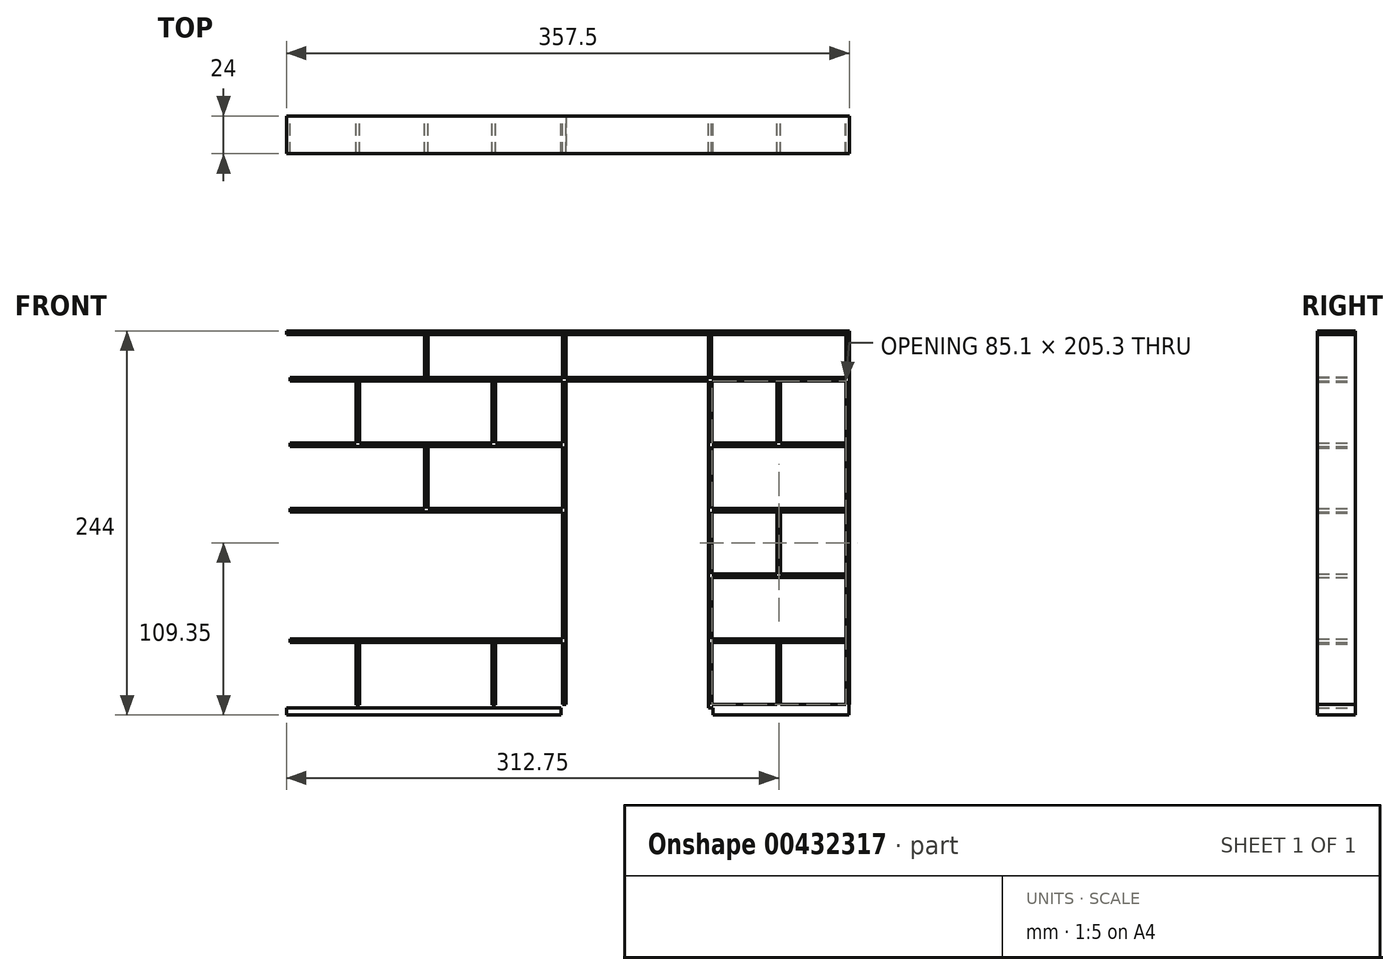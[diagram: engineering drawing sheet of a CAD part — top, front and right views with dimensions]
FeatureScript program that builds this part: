
annotation { "Feature Type Name" : "Feature", "Feature Type Description" : "" }
export const myFeature = defineFeature(function(context is Context, id is Id, definition is map)
    precondition{}
    {
        {
            var Q0;
            Q0=qCreatedBy(makeId("Front.planeOp"),FACE);
            var sketch = newSketch(context, id + "F0", { "sketchPlane" : qUnion([Q0])});
            skLineSegment(sketch, "E0", {"start": v(3.75, 85) * mm, "end": v(3.75, -122) * mm});
            skLineSegment(sketch, "E1", {"start": v(84.25, 85) * mm, "end": v(84.25, -122) * mm});
            skLineSegment(sketch, "E2", {"start": v(3.75, 85) * mm, "end": v(84.25, 85) * mm});
            skLineSegment(sketch, "E3", {"start": v(178.75, 119.8) * mm, "end": v(-178.75, 119.8) * mm});
            skLineSegment(sketch, "E4", {"start": v(-178.75, 119.8) * mm, "end": v(-178.75, 122) * mm});
            skLineSegment(sketch, "E5", {"start": v(-178.75, 122) * mm, "end": v(178.75, 122) * mm});
            skLineSegment(sketch, "E6", {"start": v(178.75, 122) * mm, "end": v(178.75, 119.8) * mm});
            skLineSegment(sketch, "E7", {"start": v(176.55, 90) * mm, "end": v(-176.55, 90) * mm});
            skLineSegment(sketch, "E8", {"start": v(-176.55, 90) * mm, "end": v(-176.55, 92.2) * mm});
            skLineSegment(sketch, "E9", {"start": v(-176.55, 92.2) * mm, "end": v(176.55, 92.2) * mm});
            skLineSegment(sketch, "E10", {"start": v(176.55, 92.2) * mm, "end": v(176.55, 90) * mm});
            skLineSegment(sketch, "E11", {"start": v(-3.45, -76) * mm, "end": v(-176.55, -76) * mm});
            skLineSegment(sketch, "E12", {"start": v(-176.55, -76) * mm, "end": v(-176.55, -73.8) * mm});
            skLineSegment(sketch, "E13", {"start": v(-176.55, -73.8) * mm, "end": v(-3.45, -73.8) * mm});
            skLineSegment(sketch, "E14", {"start": v(-3.45, -73.8) * mm, "end": v(-3.45, -76) * mm});
            skLineSegment(sketch, "E15", {"start": v(-1.25, -117.5) * mm, "end": v(-178.75, -117.5) * mm});
            skLineSegment(sketch, "E16", {"start": v(-178.75, -117.5) * mm, "end": v(-178.75, -115.3) * mm});
            skLineSegment(sketch, "E17", {"start": v(-178.75, -115.3) * mm, "end": v(-1.25, -115.3) * mm});
            skLineSegment(sketch, "E18", {"start": v(-1.25, -115.3) * mm, "end": v(-1.25, -117.5) * mm});
            skLineSegment(sketch, "E19", {"start": v(178.45, -117.5) * mm, "end": v(89.25, -117.5) * mm});
            skLineSegment(sketch, "E20", {"start": v(89.25, -117.5) * mm, "end": v(89.25, -115.3) * mm});
            skLineSegment(sketch, "E21", {"start": v(89.25, -115.3) * mm, "end": v(178.45, -115.3) * mm});
            skLineSegment(sketch, "E22", {"start": v(178.45, -115.3) * mm, "end": v(178.45, -117.5) * mm});
            skLineSegment(sketch, "E23", {"start": v(-176.55, 119.8) * mm, "end": v(-176.55, -115.3) * mm});
            skLineSegment(sketch, "E24", {"start": v(-176.55, -115.3) * mm, "end": v(-178.75, -115.3) * mm});
            skLineSegment(sketch, "E25", {"start": v(-178.75, -115.3) * mm, "end": v(-178.75, 119.8) * mm});
            skLineSegment(sketch, "E26", {"start": v(-178.75, 119.8) * mm, "end": v(-176.55, 119.8) * mm});
            skLineSegment(sketch, "E27", {"start": v(178.75, 119.8) * mm, "end": v(178.75, -115.3) * mm});
            skLineSegment(sketch, "E28", {"start": v(178.75, -115.3) * mm, "end": v(176.55, -115.3) * mm});
            skLineSegment(sketch, "E29", {"start": v(176.55, -115.3) * mm, "end": v(176.55, 119.8) * mm});
            skLineSegment(sketch, "E30", {"start": v(176.55, 119.8) * mm, "end": v(178.75, 119.8) * mm});
            skLineSegment(sketch, "E31", {"start": v(-3.45, 7) * mm, "end": v(-176.55, 7) * mm});
            skLineSegment(sketch, "E32", {"start": v(-176.55, 7) * mm, "end": v(-176.55, 9.2) * mm});
            skLineSegment(sketch, "E33", {"start": v(-176.55, 9.2) * mm, "end": v(-3.45, 9.2) * mm});
            skLineSegment(sketch, "E34", {"start": v(-3.45, 9.2) * mm, "end": v(-3.45, 7) * mm});
            skLineSegment(sketch, "E35", {"start": v(-3.45, 48.5) * mm, "end": v(-176.55, 48.5) * mm});
            skLineSegment(sketch, "E36", {"start": v(-176.55, 48.5) * mm, "end": v(-176.55, 50.7) * mm});
            skLineSegment(sketch, "E37", {"start": v(-176.55, 50.7) * mm, "end": v(-3.45, 50.7) * mm});
            skLineSegment(sketch, "E38", {"start": v(-3.45, 50.7) * mm, "end": v(-3.45, 48.5) * mm});
            skLineSegment(sketch, "E39", {"start": v(176.25, -76) * mm, "end": v(91.45, -76) * mm});
            skLineSegment(sketch, "E40", {"start": v(91.45, -76) * mm, "end": v(91.45, -73.8) * mm});
            skLineSegment(sketch, "E41", {"start": v(91.45, -73.8) * mm, "end": v(176.25, -73.8) * mm});
            skLineSegment(sketch, "E42", {"start": v(176.25, -73.8) * mm, "end": v(176.25, -76) * mm});
            skLineSegment(sketch, "E43", {"start": v(176.25, -34.5) * mm, "end": v(91.45, -34.5) * mm});
            skLineSegment(sketch, "E44", {"start": v(91.45, -34.5) * mm, "end": v(91.45, -32.3) * mm});
            skLineSegment(sketch, "E45", {"start": v(91.45, -32.3) * mm, "end": v(176.25, -32.3) * mm});
            skLineSegment(sketch, "E46", {"start": v(176.25, -32.3) * mm, "end": v(176.25, -34.5) * mm});
            skLineSegment(sketch, "E47", {"start": v(176.25, 7) * mm, "end": v(91.45, 7) * mm});
            skLineSegment(sketch, "E48", {"start": v(91.45, 7) * mm, "end": v(91.45, 9.2) * mm});
            skLineSegment(sketch, "E49", {"start": v(91.45, 9.2) * mm, "end": v(176.25, 9.2) * mm});
            skLineSegment(sketch, "E50", {"start": v(176.25, 9.2) * mm, "end": v(176.25, 7) * mm});
            skLineSegment(sketch, "E51", {"start": v(176.25, 48.5) * mm, "end": v(91.45, 48.5) * mm});
            skLineSegment(sketch, "E52", {"start": v(91.45, 48.5) * mm, "end": v(91.45, 50.7) * mm});
            skLineSegment(sketch, "E53", {"start": v(91.45, 50.7) * mm, "end": v(176.25, 50.7) * mm});
            skLineSegment(sketch, "E54", {"start": v(176.25, 50.7) * mm, "end": v(176.25, 48.5) * mm});
            skLineSegment(sketch, "E55", {"start": v(-1.25, 90) * mm, "end": v(-1.25, -115.3) * mm});
            skLineSegment(sketch, "E56", {"start": v(-1.25, -115.3) * mm, "end": v(-3.45, -115.3) * mm});
            skLineSegment(sketch, "E57", {"start": v(-3.45, -115.3) * mm, "end": v(-3.45, 90) * mm});
            skLineSegment(sketch, "E58", {"start": v(-3.45, 90) * mm, "end": v(-1.25, 90) * mm});
            skLineSegment(sketch, "E59", {"start": v(91.45, 90) * mm, "end": v(91.45, -115.3) * mm});
            skLineSegment(sketch, "E60", {"start": v(91.45, -115.3) * mm, "end": v(89.25, -115.3) * mm});
            skLineSegment(sketch, "E61", {"start": v(89.25, -115.3) * mm, "end": v(89.25, 90) * mm});
            skLineSegment(sketch, "E62", {"start": v(89.25, 90) * mm, "end": v(91.45, 90) * mm});
            skLineSegment(sketch, "E63", {"start": v(-4.25, -122) * mm, "end": v(-178.75, -122) * mm});
            skLineSegment(sketch, "E64", {"start": v(-178.75, -122) * mm, "end": v(-178.75, -117.5) * mm});
            skLineSegment(sketch, "E65", {"start": v(-178.75, -117.5) * mm, "end": v(-4.25, -117.5) * mm});
            skLineSegment(sketch, "E66", {"start": v(-4.25, -117.5) * mm, "end": v(-4.25, -122) * mm});
            skLineSegment(sketch, "E67", {"start": v(178.45, -122) * mm, "end": v(92.25, -122) * mm});
            skLineSegment(sketch, "E68", {"start": v(92.25, -122) * mm, "end": v(92.25, -117.5) * mm});
            skLineSegment(sketch, "E69", {"start": v(92.25, -117.5) * mm, "end": v(178.45, -117.5) * mm});
            skLineSegment(sketch, "E70", {"start": v(178.45, -117.5) * mm, "end": v(178.45, -122) * mm});
            skLineSegment(sketch, "E71", {"start": v(-88.74, 92.7) * mm, "end": v(-90.94, 92.7) * mm});
            skLineSegment(sketch, "E72", {"start": v(-90.94, 92.7) * mm, "end": v(-90.94, 119.47) * mm});
            skLineSegment(sketch, "E73", {"start": v(-90.94, 119.47) * mm, "end": v(-88.74, 119.47) * mm});
            skLineSegment(sketch, "E74", {"start": v(-88.74, 119.47) * mm, "end": v(-88.74, 92.7) * mm});
            skLineSegment(sketch, "E75", {"start": v(-1.25, 92.7) * mm, "end": v(-3.45, 92.7) * mm});
            skLineSegment(sketch, "E76", {"start": v(-3.45, 92.7) * mm, "end": v(-3.45, 119.47) * mm});
            skLineSegment(sketch, "E77", {"start": v(-3.45, 119.47) * mm, "end": v(-1.25, 119.47) * mm});
            skLineSegment(sketch, "E78", {"start": v(-1.25, 119.47) * mm, "end": v(-1.25, 92.7) * mm});
            skLineSegment(sketch, "E79", {"start": v(91.35, 92.7) * mm, "end": v(89.15, 92.7) * mm});
            skLineSegment(sketch, "E80", {"start": v(89.15, 92.7) * mm, "end": v(89.15, 119.47) * mm});
            skLineSegment(sketch, "E81", {"start": v(89.15, 119.47) * mm, "end": v(91.35, 119.47) * mm});
            skLineSegment(sketch, "E82", {"start": v(91.35, 119.47) * mm, "end": v(91.35, 92.7) * mm});
            skLineSegment(sketch, "E83", {"start": v(-88.74, 9.01) * mm, "end": v(-90.94, 9.01) * mm});
            skLineSegment(sketch, "E84", {"start": v(-90.94, 9.01) * mm, "end": v(-90.94, 47.71) * mm});
            skLineSegment(sketch, "E85", {"start": v(-90.94, 47.71) * mm, "end": v(-88.74, 47.71) * mm});
            skLineSegment(sketch, "E86", {"start": v(-88.74, 47.71) * mm, "end": v(-88.74, 9.01) * mm});
            skLineSegment(sketch, "E87", {"start": v(-45.84, 50.7) * mm, "end": v(-48.04, 50.7) * mm});
            skLineSegment(sketch, "E88", {"start": v(-48.04, 50.7) * mm, "end": v(-48.04, 89.4) * mm});
            skLineSegment(sketch, "E89", {"start": v(-48.04, 89.4) * mm, "end": v(-45.84, 89.4) * mm});
            skLineSegment(sketch, "E90", {"start": v(-45.84, 89.4) * mm, "end": v(-45.84, 50.7) * mm});
            skLineSegment(sketch, "E91", {"start": v(135.12, 50.7) * mm, "end": v(132.92, 50.7) * mm});
            skLineSegment(sketch, "E92", {"start": v(132.92, 50.7) * mm, "end": v(132.92, 89.4) * mm});
            skLineSegment(sketch, "E93", {"start": v(132.92, 89.4) * mm, "end": v(135.12, 89.4) * mm});
            skLineSegment(sketch, "E94", {"start": v(135.12, 89.4) * mm, "end": v(135.12, 50.7) * mm});
            skLineSegment(sketch, "E95", {"start": v(135.12, -32.38) * mm, "end": v(132.92, -32.38) * mm});
            skLineSegment(sketch, "E96", {"start": v(132.92, -32.38) * mm, "end": v(132.92, 6.32) * mm});
            skLineSegment(sketch, "E97", {"start": v(132.92, 6.32) * mm, "end": v(135.12, 6.32) * mm});
            skLineSegment(sketch, "E98", {"start": v(135.12, 6.32) * mm, "end": v(135.12, -32.38) * mm});
            skLineSegment(sketch, "E99", {"start": v(135.12, -115.46) * mm, "end": v(132.92, -115.46) * mm});
            skLineSegment(sketch, "E100", {"start": v(132.92, -115.46) * mm, "end": v(132.92, -76.76) * mm});
            skLineSegment(sketch, "E101", {"start": v(132.92, -76.76) * mm, "end": v(135.12, -76.76) * mm});
            skLineSegment(sketch, "E102", {"start": v(135.12, -76.76) * mm, "end": v(135.12, -115.46) * mm});
            skLineSegment(sketch, "E103", {"start": v(-132.2, 50.7) * mm, "end": v(-134.4, 50.7) * mm});
            skLineSegment(sketch, "E104", {"start": v(-134.4, 50.7) * mm, "end": v(-134.4, 89.4) * mm});
            skLineSegment(sketch, "E105", {"start": v(-134.4, 89.4) * mm, "end": v(-132.2, 89.4) * mm});
            skLineSegment(sketch, "E106", {"start": v(-132.2, 89.4) * mm, "end": v(-132.2, 50.7) * mm});
            skLineSegment(sketch, "E107", {"start": v(-45.84, -115.46) * mm, "end": v(-48.04, -115.46) * mm});
            skLineSegment(sketch, "E108", {"start": v(-48.04, -115.46) * mm, "end": v(-48.04, -76.76) * mm});
            skLineSegment(sketch, "E109", {"start": v(-48.04, -76.76) * mm, "end": v(-45.84, -76.76) * mm});
            skLineSegment(sketch, "E110", {"start": v(-45.84, -76.76) * mm, "end": v(-45.84, -115.46) * mm});
            skLineSegment(sketch, "E111", {"start": v(-132.2, -115.46) * mm, "end": v(-134.4, -115.46) * mm});
            skLineSegment(sketch, "E112", {"start": v(-134.4, -115.46) * mm, "end": v(-134.4, -76.76) * mm});
            skLineSegment(sketch, "E113", {"start": v(-134.4, -76.76) * mm, "end": v(-132.2, -76.76) * mm});
            skLineSegment(sketch, "E114", {"start": v(-132.2, -76.76) * mm, "end": v(-132.2, -115.46) * mm});
            skLineSegment(sketch, "E115", {"start": v(-34.3, -64.72) * mm, "end": v(-145.3, -64.72) * mm});
            skLineSegment(sketch, "E116", {"start": v(-145.3, -64.72) * mm, "end": v(-145.3, -2.72) * mm});
            skLineSegment(sketch, "E117", {"start": v(-145.3, -2.72) * mm, "end": v(-34.3, -2.72) * mm});
            skLineSegment(sketch, "E118", {"start": v(-34.3, -2.72) * mm, "end": v(-34.3, -64.72) * mm});
            skSolve(sketch);
        }
        {
            var Q0;
            Q0=makeQuery(id+"F0.imprint","IMPRINT",FACE,{"disambiguationData":[TD([[makeQuery(id+"F0.imprint","IMPRINT",EDGE,{"derivedFrom":sQuery(id+"F0.wireOp",EDGE,"E16")}),-1.0]])]});
            var Q1;
            {var subQ0=sQuery(id+"F0.wireOp",EDGE,"E50");Q1=makeQuery(id+"F0.imprint","IMPRINT",FACE,{"disambiguationData":[TD([[makeQuery(id+"F0.imprint","IMPRINT",EDGE,{"derivedFrom":subQ0}),-1.0]])]});}
            var Q2;
            {var subQ5=sQuery(id+"F0.wireOp",EDGE,"E89");Q2=makeQuery(id+"F0.imprint","IMPRINT",FACE,{"disambiguationData":[TD([[makeQuery(id+"F0.imprint","IMPRINT",EDGE,{"derivedFrom":subQ5}),-1.0]])]});}
            var Q3;
            {var subQ1=sQuery(id+"F0.wireOp",EDGE,"E24");Q3=makeQuery(id+"F0.imprint","IMPRINT",FACE,{"disambiguationData":[TD([[makeQuery(id+"F0.imprint","IMPRINT",EDGE,{"derivedFrom":subQ1}),-1.0]])]});}
            var Q4;
            {var subQ12=sQuery(id+"F0.wireOp",EDGE,"E20");Q4=makeQuery(id+"F0.imprint","IMPRINT",FACE,{"disambiguationData":[TD([[makeQuery(id+"F0.imprint","IMPRINT",EDGE,{"derivedFrom":subQ12}),-1.0]])]});}
            var Q5;
            {var subQ2=sQuery(id+"F0.wireOp",EDGE,"E35");Q5=makeQuery(id+"F0.imprint","IMPRINT",FACE,{"disambiguationData":[TD([[makeQuery(id+"F0.imprint","IMPRINT",EDGE,{"derivedFrom":subQ2}),-1.0]])]});}
            var Q6;
            {var subQ0=sQuery(id+"F0.wireOp",EDGE,"E42");Q6=makeQuery(id+"F0.imprint","IMPRINT",FACE,{"disambiguationData":[TD([[makeQuery(id+"F0.imprint","IMPRINT",EDGE,{"derivedFrom":subQ0}),-1.0]])]});}
            var Q7;
            Q7=makeQuery(id+"F0.imprint","IMPRINT",FACE,{"disambiguationData":[TD([[makeQuery(id+"F0.imprint","IMPRINT",EDGE,{"derivedFrom":sQuery(id+"F0.wireOp",EDGE,"E55")}),-1.0]])]});
            var Q8;
            {var subQ5=sQuery(id+"F0.wireOp",EDGE,"E93");Q8=makeQuery(id+"F0.imprint","IMPRINT",FACE,{"disambiguationData":[TD([[makeQuery(id+"F0.imprint","IMPRINT",EDGE,{"derivedFrom":subQ5}),-1.0]])]});}
            var Q9;
            {var subQ19=sQuery(id+"F0.wireOp",EDGE,"E40");Q9=makeQuery(id+"F0.imprint","IMPRINT",FACE,{"disambiguationData":[TD([[makeQuery(id+"F0.imprint","IMPRINT",EDGE,{"derivedFrom":subQ19}),1.0]])]});}
            var Q10;
            {var subQ8=sQuery(id+"F0.wireOp",EDGE,"E31");Q10=makeQuery(id+"F0.imprint","IMPRINT",FACE,{"disambiguationData":[TD([[makeQuery(id+"F0.imprint","IMPRINT",EDGE,{"derivedFrom":subQ8}),-1.0]])]});}
            var Q11;
            {var subQ5=sQuery(id+"F0.wireOp",EDGE,"E85");Q11=makeQuery(id+"F0.imprint","IMPRINT",FACE,{"disambiguationData":[TD([[makeQuery(id+"F0.imprint","IMPRINT",EDGE,{"derivedFrom":subQ5}),-1.0]])]});}
            var Q12;
            {var subQ5=sQuery(id+"F0.wireOp",EDGE,"E101");Q12=makeQuery(id+"F0.imprint","IMPRINT",FACE,{"disambiguationData":[TD([[makeQuery(id+"F0.imprint","IMPRINT",EDGE,{"derivedFrom":subQ5}),-1.0]])]});}
            var Q13;
            {var subQ0=sQuery(id+"F0.wireOp",EDGE,"E46");Q13=makeQuery(id+"F0.imprint","IMPRINT",FACE,{"disambiguationData":[TD([[makeQuery(id+"F0.imprint","IMPRINT",EDGE,{"derivedFrom":subQ0}),-1.0]])]});}
            var Q14;
            Q14=makeQuery(id+"F0.imprint","IMPRINT",FACE,{"disambiguationData":[TD([[makeQuery(id+"F0.imprint","IMPRINT",EDGE,{"derivedFrom":sQuery(id+"F0.wireOp",EDGE,"E3")}),-1.0]])]});
            var Q15;
            Q15=makeQuery(id+"F0.imprint","IMPRINT",FACE,{"disambiguationData":[TD([[makeQuery(id+"F0.imprint","IMPRINT",EDGE,{"derivedFrom":sQuery(id+"F0.wireOp",EDGE,"E71")}),-1.0]])]});
            var Q16;
            Q16=makeQuery(id+"F0.imprint","IMPRINT",FACE,{"disambiguationData":[TD([[makeQuery(id+"F0.imprint","IMPRINT",EDGE,{"derivedFrom":sQuery(id+"F0.wireOp",EDGE,"E75")}),-1.0]])]});
            var Q17;
            Q17=makeQuery(id+"F0.imprint","IMPRINT",FACE,{"disambiguationData":[TD([[makeQuery(id+"F0.imprint","IMPRINT",EDGE,{"derivedFrom":sQuery(id+"F0.wireOp",EDGE,"E79")}),-1.0]])]});
            var Q18;
            {var subQ5=sQuery(id+"F0.wireOp",EDGE,"E63");Q18=makeQuery(id+"F0.imprint","IMPRINT",FACE,{"disambiguationData":[TD([[makeQuery(id+"F0.imprint","IMPRINT",EDGE,{"derivedFrom":subQ5}),-1.0]])]});}
            var Q19;
            {var subQ5=sQuery(id+"F0.wireOp",EDGE,"E67");Q19=makeQuery(id+"F0.imprint","IMPRINT",FACE,{"disambiguationData":[TD([[makeQuery(id+"F0.imprint","IMPRINT",EDGE,{"derivedFrom":subQ5}),-1.0]])]});}
            var Q20;
            {var subQ5=sQuery(id+"F0.wireOp",EDGE,"E113");Q20=makeQuery(id+"F0.imprint","IMPRINT",FACE,{"disambiguationData":[TD([[makeQuery(id+"F0.imprint","IMPRINT",EDGE,{"derivedFrom":subQ5}),-1.0]])]});}
            var Q21;
            {var subQ5=sQuery(id+"F0.wireOp",EDGE,"E109");Q21=makeQuery(id+"F0.imprint","IMPRINT",FACE,{"disambiguationData":[TD([[makeQuery(id+"F0.imprint","IMPRINT",EDGE,{"derivedFrom":subQ5}),-1.0]])]});}
            var Q22;
            {var subQ0=sQuery(id+"F0.wireOp",EDGE,"E9");Q22=makeQuery(id+"F0.imprint","IMPRINT",FACE,{"disambiguationData":[TD([[makeQuery(id+"F0.imprint","IMPRINT",EDGE,{"derivedFrom":subQ0}),-1.0]])]});}
            var Q23;
            {var subQ0=sQuery(id+"F0.wireOp",EDGE,"E54");Q23=makeQuery(id+"F0.imprint","IMPRINT",FACE,{"disambiguationData":[TD([[makeQuery(id+"F0.imprint","IMPRINT",EDGE,{"derivedFrom":subQ0}),-1.0]])]});}
            var Q24;
            {var subQ5=sQuery(id+"F0.wireOp",EDGE,"E105");Q24=makeQuery(id+"F0.imprint","IMPRINT",FACE,{"disambiguationData":[TD([[makeQuery(id+"F0.imprint","IMPRINT",EDGE,{"derivedFrom":subQ5}),-1.0]])]});}
            var Q25;
            {var subQ0=sQuery(id+"F0.wireOp",EDGE,"E11");Q25=makeQuery(id+"F0.imprint","IMPRINT",FACE,{"disambiguationData":[TD([[makeQuery(id+"F0.imprint","IMPRINT",EDGE,{"derivedFrom":subQ0}),-1.0]])]});}
            var Q26;
            {var subQ5=sQuery(id+"F0.wireOp",EDGE,"E27");Q26=makeQuery(id+"F0.imprint","IMPRINT",FACE,{"disambiguationData":[TD([[makeQuery(id+"F0.imprint","IMPRINT",EDGE,{"derivedFrom":subQ5}),-1.0]])]});}
            var Q27;
            {var subQ5=sQuery(id+"F0.wireOp",EDGE,"E97");Q27=makeQuery(id+"F0.imprint","IMPRINT",FACE,{"disambiguationData":[TD([[makeQuery(id+"F0.imprint","IMPRINT",EDGE,{"derivedFrom":subQ5}),-1.0]])]});}
            var Q28;
            {var subQ5=sQuery(id+"F0.wireOp",EDGE,"E65");Q28=makeQuery(id+"F0.imprint","IMPRINT",FACE,{"disambiguationData":[TD([[makeQuery(id+"F0.imprint","IMPRINT",EDGE,{"derivedFrom":subQ5}),-1.0]])]});}
            var Q29;
            {var subQ5=sQuery(id+"F0.wireOp",EDGE,"E69");Q29=makeQuery(id+"F0.imprint","IMPRINT",FACE,{"disambiguationData":[TD([[makeQuery(id+"F0.imprint","IMPRINT",EDGE,{"derivedFrom":subQ5}),-1.0]])]});}
            var Q30;
            {var subQ5=sQuery(id+"F0.wireOp",EDGE,"E87");Q30=makeQuery(id+"F0.imprint","IMPRINT",FACE,{"disambiguationData":[TD([[makeQuery(id+"F0.imprint","IMPRINT",EDGE,{"derivedFrom":subQ5}),-1.0]])]});}
            var Q31;
            {var subQ5=sQuery(id+"F0.wireOp",EDGE,"E91");Q31=makeQuery(id+"F0.imprint","IMPRINT",FACE,{"disambiguationData":[TD([[makeQuery(id+"F0.imprint","IMPRINT",EDGE,{"derivedFrom":subQ5}),-1.0]])]});}
            var Q32;
            {var subQ0=sQuery(id+"F0.wireOp",EDGE,"E48");Q32=makeQuery(id+"F0.imprint","IMPRINT",FACE,{"disambiguationData":[TD([[makeQuery(id+"F0.imprint","IMPRINT",EDGE,{"derivedFrom":subQ0}),-1.0]])]});}
            var Q33;
            {var subQ0=sQuery(id+"F0.wireOp",EDGE,"E52");Q33=makeQuery(id+"F0.imprint","IMPRINT",FACE,{"disambiguationData":[TD([[makeQuery(id+"F0.imprint","IMPRINT",EDGE,{"derivedFrom":subQ0}),-1.0]])]});}
            var Q34;
            {var subQ0=sQuery(id+"F0.wireOp",EDGE,"E40");Q34=makeQuery(id+"F0.imprint","IMPRINT",FACE,{"disambiguationData":[TD([[makeQuery(id+"F0.imprint","IMPRINT",EDGE,{"derivedFrom":subQ0}),-1.0]])]});}
            var Q35;
            {var subQ5=sQuery(id+"F0.wireOp",EDGE,"E83");Q35=makeQuery(id+"F0.imprint","IMPRINT",FACE,{"disambiguationData":[TD([[makeQuery(id+"F0.imprint","IMPRINT",EDGE,{"derivedFrom":subQ5}),-1.0]])]});}
            var Q36;
            {var subQ5=sQuery(id+"F0.wireOp",EDGE,"E99");Q36=makeQuery(id+"F0.imprint","IMPRINT",FACE,{"disambiguationData":[TD([[makeQuery(id+"F0.imprint","IMPRINT",EDGE,{"derivedFrom":subQ5}),-1.0]])]});}
            var Q37;
            {var subQ5=sQuery(id+"F0.wireOp",EDGE,"E111");Q37=makeQuery(id+"F0.imprint","IMPRINT",FACE,{"disambiguationData":[TD([[makeQuery(id+"F0.imprint","IMPRINT",EDGE,{"derivedFrom":subQ5}),-1.0]])]});}
            var Q38;
            {var subQ5=sQuery(id+"F0.wireOp",EDGE,"E107");Q38=makeQuery(id+"F0.imprint","IMPRINT",FACE,{"disambiguationData":[TD([[makeQuery(id+"F0.imprint","IMPRINT",EDGE,{"derivedFrom":subQ5}),-1.0]])]});}
            var Q39;
            {var subQ0=sQuery(id+"F0.wireOp",EDGE,"E44");Q39=makeQuery(id+"F0.imprint","IMPRINT",FACE,{"disambiguationData":[TD([[makeQuery(id+"F0.imprint","IMPRINT",EDGE,{"derivedFrom":subQ0}),-1.0]])]});}
            var Q40;
            {var subQ5=sQuery(id+"F0.wireOp",EDGE,"E103");Q40=makeQuery(id+"F0.imprint","IMPRINT",FACE,{"disambiguationData":[TD([[makeQuery(id+"F0.imprint","IMPRINT",EDGE,{"derivedFrom":subQ5}),-1.0]])]});}
            var Q41;
            {var subQ5=sQuery(id+"F0.wireOp",EDGE,"E95");Q41=makeQuery(id+"F0.imprint","IMPRINT",FACE,{"disambiguationData":[TD([[makeQuery(id+"F0.imprint","IMPRINT",EDGE,{"derivedFrom":subQ5}),-1.0]])]});}
            extrude(context, id + "F1", {"entities" : qUnion([Q0, Q1, Q2, Q3, Q4, Q5, Q6, Q7, Q8, Q9, Q10, Q11, Q12, Q13, Q14, Q15, Q16, Q17, Q18, Q19, Q20, Q21, Q22, Q23, Q24, Q25, Q26, Q27, Q28, Q29, Q30, Q31, Q32, Q33, Q34, Q35, Q36, Q37, Q38, Q39, Q40, Q41]), "depth" : 24 * mm});
        }
    });
